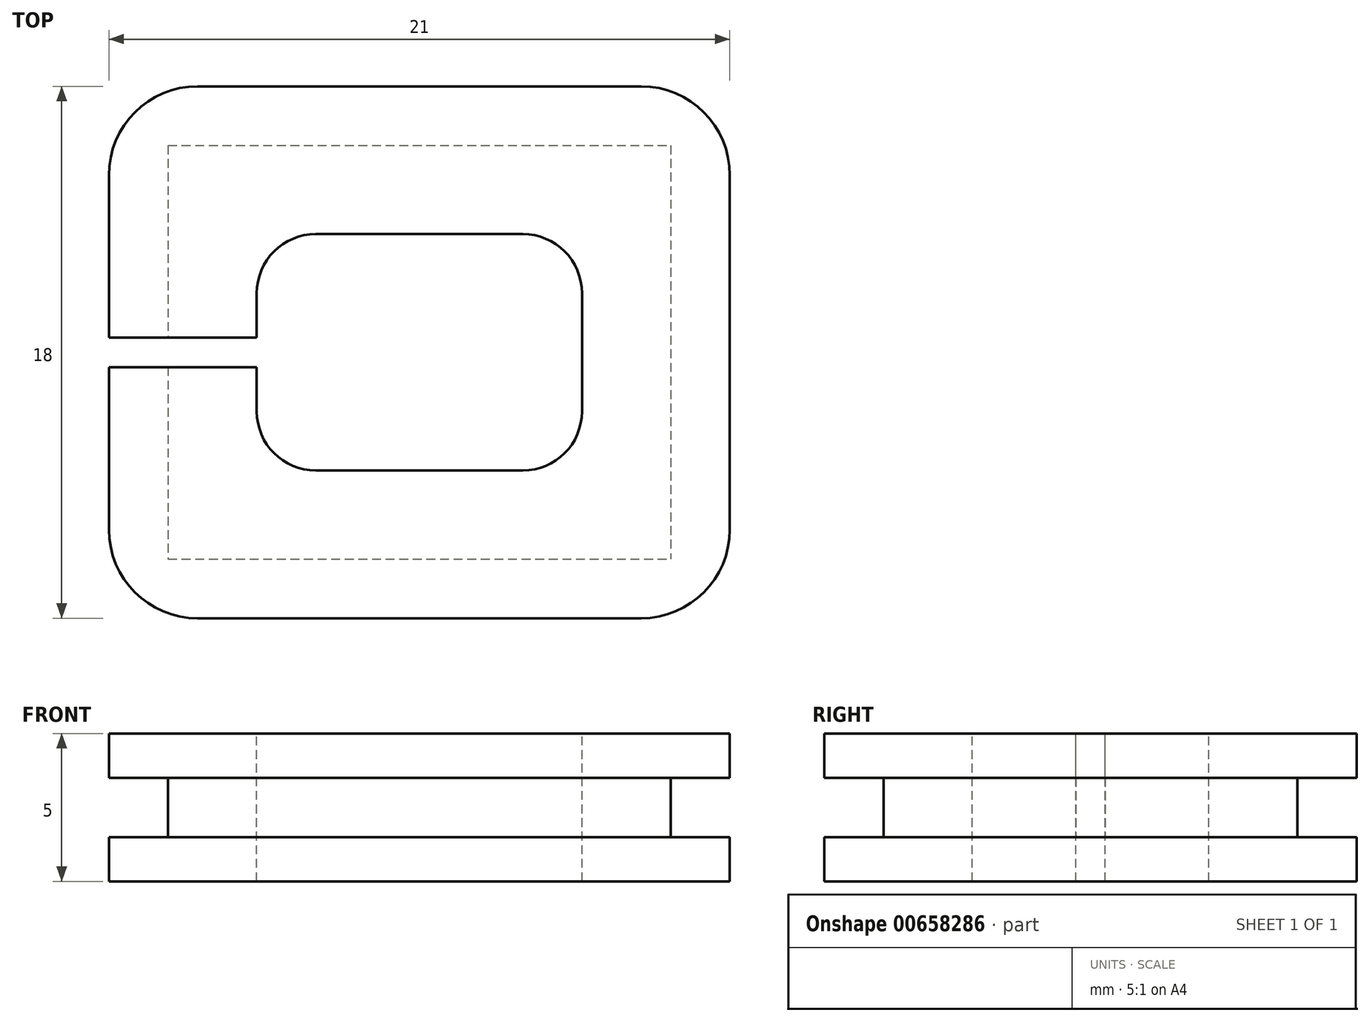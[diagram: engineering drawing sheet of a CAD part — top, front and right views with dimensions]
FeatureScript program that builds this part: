
annotation { "Feature Type Name" : "Feature", "Feature Type Description" : "" }
export const myFeature = defineFeature(function(context is Context, id is Id, definition is map)
    precondition{}
    {
        {
            var Q0;
            Q0=qCreatedBy(makeId("Top.planeOp"),FACE);
            var sketch = newSketch(context, id + "F0", { "sketchPlane" : qUnion([Q0])});
            skLineSegment(sketch, "E0.bottom", {"start": v(-8.5, 7) * mm, "end": v(8.5, 7) * mm});
            skLineSegment(sketch, "E0.top", {"start": v(-8.5, -7) * mm, "end": v(8.5, -7) * mm});
            skLineSegment(sketch, "E0.left", {"start": v(-8.5, 7) * mm, "end": v(-8.5, -7) * mm});
            skLineSegment(sketch, "E0.right", {"start": v(8.5, 7) * mm, "end": v(8.5, -7) * mm});
            skPoint(sketch, "E0.middle", {"position": v(0, 0) * mm});
            skLineSegment(sketch, "E1.0", {"start": v(-10.5, 9) * mm, "end": v(10.5, 9) * mm});
            skLineSegment(sketch, "E1.1", {"start": v(-10.5, 9) * mm, "end": v(-10.5, -9) * mm});
            skLineSegment(sketch, "E1.2", {"start": v(-10.5, -9) * mm, "end": v(10.5, -9) * mm});
            skLineSegment(sketch, "E1.3", {"start": v(10.5, 9) * mm, "end": v(10.5, -9) * mm});
            skSolve(sketch);
        }
        {
            var Q0;
            Q0=makeQuery(id+"F0.imprint","IMPRINT",FACE,{"disambiguationData":[TD([[makeQuery(id+"F0.imprint","IMPRINT",EDGE,{"derivedFrom":sQuery(id+"F0.wireOp",EDGE,"E0.bottom")}),-1.0]])]});
            var Q1;
            Q1=makeQuery(id+"F0.imprint","IMPRINT",FACE,{"disambiguationData":[TD([[makeQuery(id+"F0.imprint","IMPRINT",EDGE,{"derivedFrom":sQuery(id+"F0.wireOp",EDGE,"E0.bottom")}),1.0]])]});
            extrude(context, id + "F1", {"entities" : qUnion([Q0, Q1]), "endBound" : BoundingType.SYMMETRIC, "depth" : 5 * mm, "offsetDistance" : 25 * mm});
        }
        {
            var Q0;
            {var subQ0=sQuery(id+"F0.wireOp",EDGE,"E1.3");var subQ1=sQuery(id+"F0.wireOp",EDGE,"E1.2");var subQ2=sQuery(id+"F0.wireOp",EDGE,"E1.1");var subQ3=sQuery(id+"F0.wireOp",EDGE,"E1.0");Q0=makeQuery(id+"F3.boolean.opBoolean","SPLIT",EDGE,{"disambiguationData":[TD([makeQuery(id+"F1.opExtrude","CAP_FACE",FACE,{"disambiguationData":[OSD([subQ3,subQ2,subQ1,subQ0])],"isStart":false})])],"derivedFrom":makeQuery(id+"F1.opExtrude","SWEPT_EDGE",EDGE,{"disambiguationData":[OSD([subQ1,subQ0])]})});}
            var Q1;
            Q1=makeQuery(id+"F1.opExtrude","SWEPT_EDGE",EDGE,{"disambiguationData":[OSD([sQuery(id+"F0.wireOp",EDGE,"E1.0"),sQuery(id+"F0.wireOp",EDGE,"E1.3")])]});
            var Q2;
            Q2=makeQuery(id+"F1.opExtrude","SWEPT_EDGE",EDGE,{"disambiguationData":[OSD([sQuery(id+"F0.wireOp",EDGE,"E1.0"),sQuery(id+"F0.wireOp",EDGE,"E1.1")])]});
            var Q3;
            Q3=makeQuery(id+"F1.opExtrude","SWEPT_EDGE",EDGE,{"disambiguationData":[OSD([sQuery(id+"F0.wireOp",EDGE,"E1.1"),sQuery(id+"F0.wireOp",EDGE,"E1.2")])]});
            fillet(context, id + "F2", {"entities" : qUnion([Q0, Q1, Q2, Q3]), "radius" : 3 * mm, "tangentPropagation" : true, "allowEdgeOverflow" : false});
        }
        {
            var Q0;
            Q0=makeQuery(id+"F0.imprint","IMPRINT",FACE,{"disambiguationData":[TD([[makeQuery(id+"F0.imprint","IMPRINT",EDGE,{"derivedFrom":sQuery(id+"F0.wireOp",EDGE,"E0.bottom")}),1.0]])]});
            extrude(context, id + "F3", {"entities" : qUnion([Q0]), "operationType" : NewBodyOperationType.REMOVE, "endBound" : BoundingType.SYMMETRIC, "oppositeDirection" : true, "depth" : 2 * mm, "offsetDistance" : 25 * mm});
        }
        {
            var Q0;
            Q0=makeQuery(id+"F1.opExtrude","CAP_FACE",FACE,{"disambiguationData":[OSD([sQuery(id+"F0.wireOp",EDGE,"E1.0"),sQuery(id+"F0.wireOp",EDGE,"E1.1"),sQuery(id+"F0.wireOp",EDGE,"E1.2"),sQuery(id+"F0.wireOp",EDGE,"E1.3")])],"isStart":false});
            var sketch = newSketch(context, id + "F4", { "sketchPlane" : qUnion([Q0])});
            skLineSegment(sketch, "E2.0", {"start": v(-5.5, -4) * mm, "end": v(5.5, -4) * mm});
            skLineSegment(sketch, "E2.1", {"start": v(-5.5, 4) * mm, "end": v(-5.5, -4) * mm});
            skLineSegment(sketch, "E2.2", {"start": v(-5.5, 4) * mm, "end": v(5.5, 4) * mm});
            skLineSegment(sketch, "E2.3", {"start": v(5.5, 4) * mm, "end": v(5.5, -4) * mm});
            skLineSegment(sketch, "E3", {"start": v(-5.5, -0.5) * mm, "end": v(-10.5, -0.5) * mm});
            skLineSegment(sketch, "E4", {"start": v(0, 0) * mm, "end": v(-10.5, 0) * mm, "construction": true});
            skLineSegment(sketch, "E5", {"start": v(-5.5, 0.5) * mm, "end": v(-10.5, 0.5) * mm});
            skSolve(sketch);
        }
        {
            var Q0;
            Q0 = qSketchRegion(id + "F4", true);
            var Q1;
            {var subQ0=sQuery(id+"F4.wireOp",EDGE,"E3");Q1=makeQuery(id+"F4.imprint","IMPRINT",FACE,{"disambiguationData":[TD([[makeQuery(id+"F4.imprint","IMPRINT",EDGE,{"derivedFrom":subQ0}),-1.0]])]});}
            extrude(context, id + "F5", {"entities" : qUnion([Q0, Q1]), "operationType" : NewBodyOperationType.REMOVE, "oppositeDirection" : true, "depth" : 25 * mm, "offsetDistance" : 25 * mm});
        }
        {
            var Q0;
            Q0=makeQuery(id+"F5.boolean.opBoolean","COPY",EDGE,{"derivedFrom":makeQuery(id+"F5.opExtrude","SWEPT_EDGE",EDGE,{"disambiguationData":[OSD([sQuery(id+"F4.wireOp",EDGE,"E2.0"),sQuery(id+"F4.wireOp",EDGE,"E2.1")])]})});
            var Q1;
            Q1=makeQuery(id+"F5.boolean.opBoolean","COPY",EDGE,{"derivedFrom":makeQuery(id+"F5.opExtrude","SWEPT_EDGE",EDGE,{"disambiguationData":[OSD([sQuery(id+"F4.wireOp",EDGE,"E2.0"),sQuery(id+"F4.wireOp",EDGE,"E2.3")])]})});
            var Q2;
            Q2=makeQuery(id+"F5.boolean.opBoolean","COPY",EDGE,{"derivedFrom":makeQuery(id+"F5.opExtrude","SWEPT_EDGE",EDGE,{"disambiguationData":[OSD([sQuery(id+"F4.wireOp",EDGE,"E2.2"),sQuery(id+"F4.wireOp",EDGE,"E2.3")])]})});
            var Q3;
            Q3=makeQuery(id+"F5.boolean.opBoolean","COPY",EDGE,{"derivedFrom":makeQuery(id+"F5.opExtrude","SWEPT_EDGE",EDGE,{"disambiguationData":[OSD([sQuery(id+"F4.wireOp",EDGE,"E2.1"),sQuery(id+"F4.wireOp",EDGE,"E2.2")])]})});
            fillet(context, id + "F6", {"entities" : qUnion([Q0, Q1, Q2, Q3]), "radius" : 2 * mm, "tangentPropagation" : true, "allowEdgeOverflow" : false});
        }
    });
